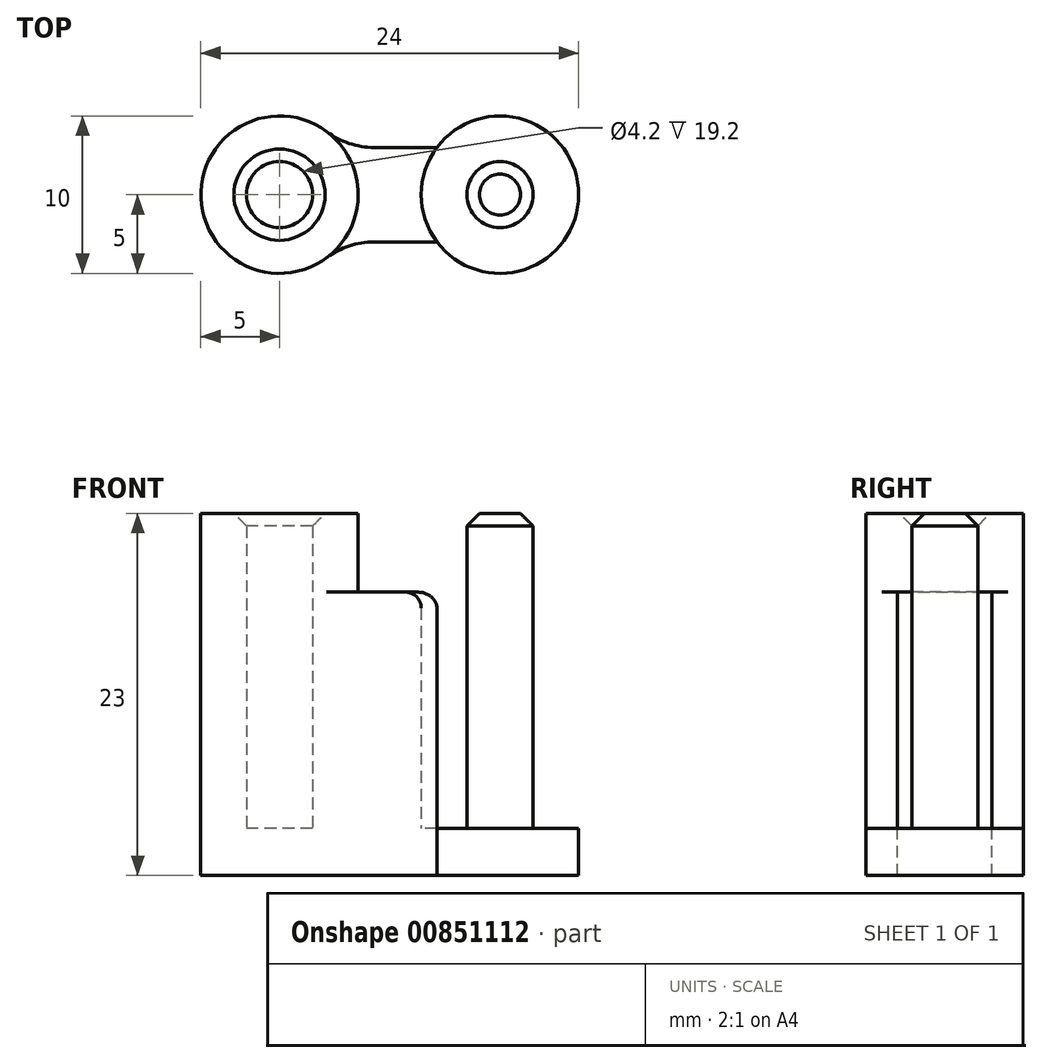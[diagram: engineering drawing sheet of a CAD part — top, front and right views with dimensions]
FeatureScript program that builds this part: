
annotation { "Feature Type Name" : "Feature", "Feature Type Description" : "" }
export const myFeature = defineFeature(function(context is Context, id is Id, definition is map)
    precondition{}
    {
        {
            var Q0;
            Q0=qCreatedBy(makeId("Top.planeOp"),FACE);
            var sketch = newSketch(context, id + "F0", { "sketchPlane" : qUnion([Q0])});
            skCircle(sketch, "E0", {"center": v(-7, 0) * mm, "radius": 2.1 * mm});
            skCircle(sketch, "E1", {"center": v(-7, 0) * mm, "radius": 5 * mm});
            skLineSegment(sketch, "E2.bottom", {"start": v(-3, 3) * mm, "end": v(0, 3) * mm});
            skLineSegment(sketch, "E2.top", {"start": v(-3, -3) * mm, "end": v(0, -3) * mm});
            skLineSegment(sketch, "E2.right", {"start": v(0, 3) * mm, "end": v(0, -3) * mm});
            skCircle(sketch, "E3.MirrorC", {"center": v(7, 0) * mm, "radius": 2.1 * mm});
            skCircle(sketch, "E4.MirrorC", {"center": v(7, 0) * mm, "radius": 5 * mm});
            skLineSegment(sketch, "E5.MirrorCS", {"start": v(3, -3) * mm, "end": v(0, -3) * mm});
            skLineSegment(sketch, "E6.MirrorCS", {"start": v(3, 3) * mm, "end": v(0, 3) * mm});
            skSolve(sketch);
        }
        {
            var Q0;
            {var subQ0=sQuery(id+"F0.wireOp",EDGE,"E2.bottom");Q0=makeQuery(id+"F0.imprint","IMPRINT",FACE,{"disambiguationData":[TD([[makeQuery(id+"F0.imprint","IMPRINT",EDGE,{"derivedFrom":subQ0}),-1.0]])]});}
            var Q1;
            Q1=makeQuery(id+"F0.imprint","IMPRINT",FACE,{"disambiguationData":[TD([[makeQuery(id+"F0.imprint","IMPRINT",EDGE,{"derivedFrom":sQuery(id+"F0.wireOp",EDGE,"E2.right")}),1.0]])]});
            var Q2;
            Q2=sQuery(id+"F0.wireOp",VERTEX,"E2.top.end");
            extrude(context, id + "F1", {"entities" : qUnion([Q0, Q1]), "depth" : 15 * mm, "endBoundEntityVertex" : qUnion([Q2]), "offsetDistance" : 25 * mm});
        }
        {
            var Q0;
            Q0=makeQuery(id+"F0.imprint","IMPRINT",FACE,{"disambiguationData":[TD([[makeQuery(id+"F0.imprint","IMPRINT",EDGE,{"derivedFrom":sQuery(id+"F0.wireOp",EDGE,"E3.MirrorC")}),1.0]])]});
            var Q1;
            Q1=makeQuery(id+"F0.imprint","IMPRINT",FACE,{"disambiguationData":[TD([[makeQuery(id+"F0.imprint","IMPRINT",EDGE,{"derivedFrom":sQuery(id+"F0.wireOp",EDGE,"E0")}),-1.0]])]});
            extrude(context, id + "F2", {"entities" : qUnion([Q0, Q1]), "operationType" : NewBodyOperationType.ADD, "depth" : 20 * mm, "offsetDistance" : 25 * mm});
        }
        {
            var Q0;
            Q0=makeQuery(id+"F0.imprint","IMPRINT",FACE,{"disambiguationData":[TD([[makeQuery(id+"F0.imprint","IMPRINT",EDGE,{"derivedFrom":sQuery(id+"F0.wireOp",EDGE,"E3.MirrorC")}),1.0]])]});
            var Q1;
            Q1=makeQuery(id+"F0.imprint","IMPRINT",FACE,{"disambiguationData":[TD([[makeQuery(id+"F0.imprint","IMPRINT",EDGE,{"derivedFrom":sQuery(id+"F0.wireOp",EDGE,"E3.MirrorC")}),-1.0]])]});
            var Q2;
            Q2=makeQuery(id+"F0.imprint","IMPRINT",FACE,{"disambiguationData":[TD([[makeQuery(id+"F0.imprint","IMPRINT",EDGE,{"derivedFrom":sQuery(id+"F0.wireOp",EDGE,"E0")}),-1.0]])]});
            var Q3;
            Q3=makeQuery(id+"F0.imprint","IMPRINT",FACE,{"disambiguationData":[TD([[makeQuery(id+"F0.imprint","IMPRINT",EDGE,{"derivedFrom":sQuery(id+"F0.wireOp",EDGE,"E0")}),1.0]])]});
            var Q4;
            Q4=makeQuery(id+"F0.imprint","IMPRINT",FACE,{"disambiguationData":[TD([[makeQuery(id+"F0.imprint","IMPRINT",EDGE,{"derivedFrom":sQuery(id+"F0.wireOp",EDGE,"E2.right")}),1.0]])]});
            var Q5;
            {var subQ0=sQuery(id+"F0.wireOp",EDGE,"E2.bottom");Q5=makeQuery(id+"F0.imprint","IMPRINT",FACE,{"disambiguationData":[TD([[makeQuery(id+"F0.imprint","IMPRINT",EDGE,{"derivedFrom":subQ0}),-1.0]])]});}
            extrude(context, id + "F3", {"entities" : qUnion([Q0, Q1, Q2, Q3, Q4, Q5]), "operationType" : NewBodyOperationType.ADD, "oppositeDirection" : true, "depth" : 3 * mm, "offsetDistance" : 25 * mm});
        }
        {
            var Q0;
            {var subQ0=sQuery(id+"F0.wireOp",EDGE,"E5.MirrorCS");var subQ1=sQuery(id+"F0.wireOp",EDGE,"E4.MirrorC");Q0=makeQuery(id+"F3.boolean.opBoolean","MERGE",EDGE,{"derivedFrom":[makeQuery(id+"F1.opExtrude","SWEPT_EDGE",EDGE,{"disambiguationData":[OSD([subQ1,subQ0])]}),makeQuery(id+"F3.opExtrude","SWEPT_EDGE",EDGE,{"disambiguationData":[OSD([subQ1,subQ0])]})]});}
            var Q1;
            {var subQ0=sQuery(id+"F0.wireOp",EDGE,"E2.top");var subQ1=sQuery(id+"F0.wireOp",EDGE,"E1");Q1=makeQuery(id+"F3.boolean.opBoolean","MERGE",EDGE,{"derivedFrom":[makeQuery(id+"F1.opExtrude","SWEPT_EDGE",EDGE,{"disambiguationData":[OSD([subQ1,subQ0])]}),makeQuery(id+"F3.opExtrude","SWEPT_EDGE",EDGE,{"disambiguationData":[OSD([subQ1,subQ0])]})]});}
            var Q2;
            {var subQ0=sQuery(id+"F0.wireOp",EDGE,"E2.bottom");var subQ1=sQuery(id+"F0.wireOp",EDGE,"E1");Q2=makeQuery(id+"F3.boolean.opBoolean","MERGE",EDGE,{"derivedFrom":[makeQuery(id+"F1.opExtrude","SWEPT_EDGE",EDGE,{"disambiguationData":[OSD([subQ1,subQ0])]}),makeQuery(id+"F3.opExtrude","SWEPT_EDGE",EDGE,{"disambiguationData":[OSD([subQ1,subQ0])]})]});}
            var Q3;
            {var subQ0=sQuery(id+"F0.wireOp",EDGE,"E6.MirrorCS");var subQ1=sQuery(id+"F0.wireOp",EDGE,"E4.MirrorC");Q3=makeQuery(id+"F3.boolean.opBoolean","MERGE",EDGE,{"derivedFrom":[makeQuery(id+"F1.opExtrude","SWEPT_EDGE",EDGE,{"disambiguationData":[OSD([subQ1,subQ0])]}),makeQuery(id+"F3.opExtrude","SWEPT_EDGE",EDGE,{"disambiguationData":[OSD([subQ1,subQ0])]})]});}
            fillet(context, id + "F4", {"entities" : qUnion([Q0, Q1, Q2, Q3]), "radius" : 5 * mm, "tangentPropagation" : true, "allowEdgeOverflow" : false});
        }
        {
            var Q0;
            Q0=makeQuery(id+"F1.opExtrude","CAP_EDGE",EDGE,{"disambiguationData":[OSD([sQuery(id+"F0.wireOp",EDGE,"E4.MirrorC")])],"isStart":false});
            var Q1;
            Q1=makeQuery(id+"F1.opExtrude","CAP_EDGE",EDGE,{"disambiguationData":[OSD([sQuery(id+"F0.wireOp",EDGE,"E1")])],"isStart":false});
            fillet(context, id + "F5", {"entities" : qUnion([Q0, Q1]), "radius" : 1 * mm, "tangentPropagation" : true, "allowEdgeOverflow" : false});
        }
        {
            var Q0;
            Q0=makeQuery(id+"F2.opExtrude","CAP_EDGE",EDGE,{"disambiguationData":[OSD([sQuery(id+"F0.wireOp",EDGE,"E0")])],"isStart":false});
            var Q1;
            Q1=makeQuery(id+"F2.opExtrude","CAP_EDGE",EDGE,{"disambiguationData":[OSD([sQuery(id+"F0.wireOp",EDGE,"E3.MirrorC")])],"isStart":false});
            chamfer(context, id + "F6", {"entities" : qUnion([Q0, Q1]), "width" : 0.8 * mm, "tangentPropagation" : true});
        }
    });
